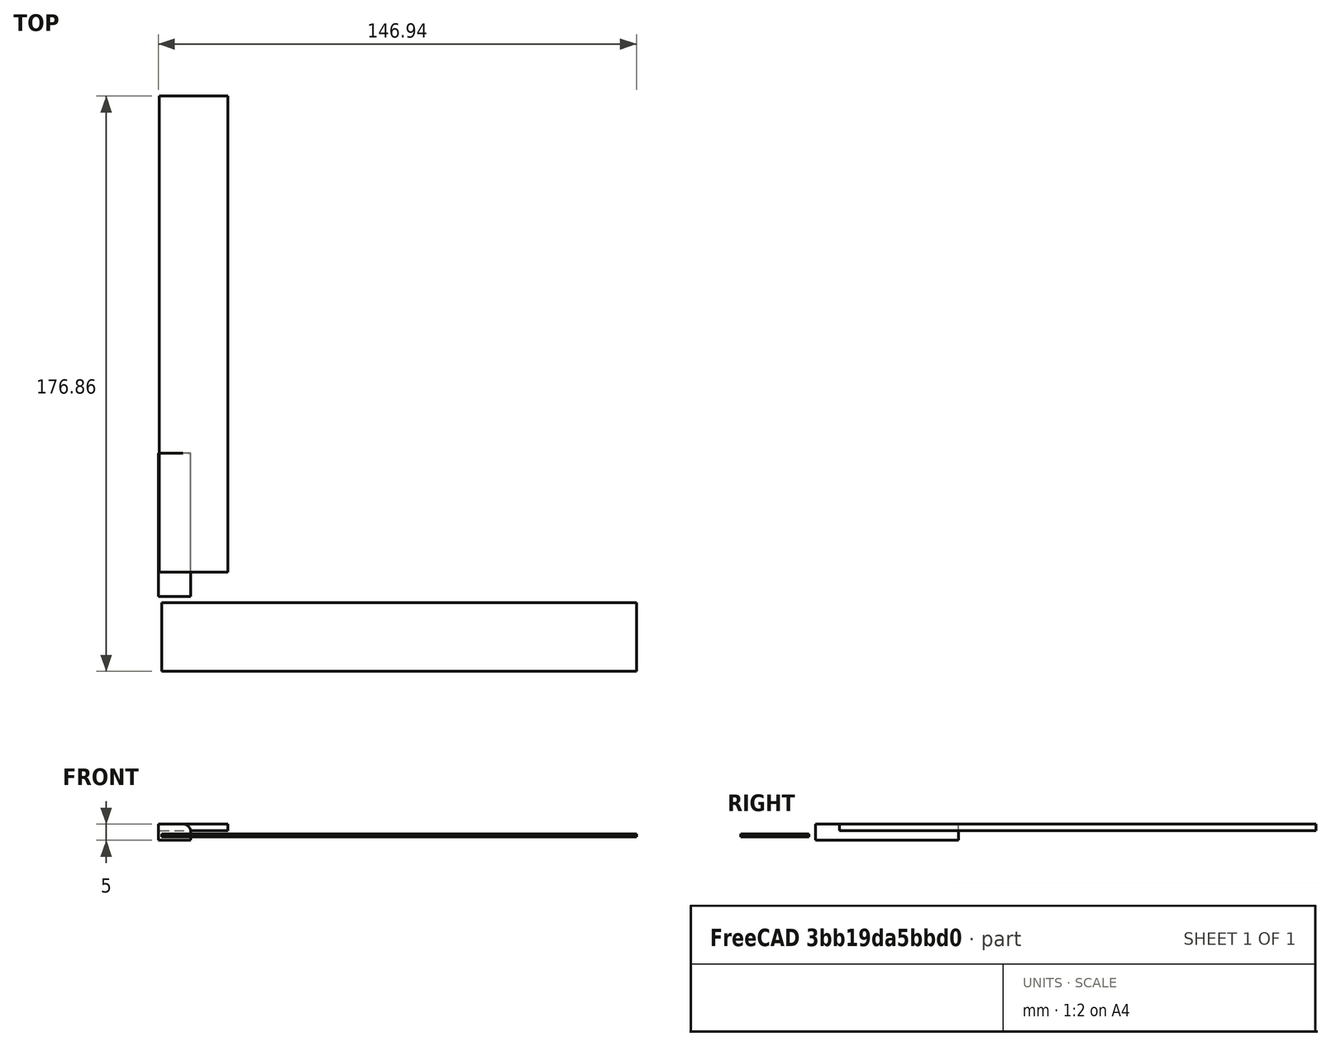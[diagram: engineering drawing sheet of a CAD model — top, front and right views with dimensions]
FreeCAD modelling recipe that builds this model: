
FCSTD DOCUMENT  (FreeCAD 0.18R4 (GitTag))
Label: UhrzeitImKlartext
License: All rights reserved
LicenseURL: http://en.wikipedia.org/wiki/All_rights_reserved
objects: Path::FeaturePython×6, Part::Part2DObjectPython×4, App::FeaturePython×2, App::DocumentObjectGroup×2, Part::FeaturePython×2, Path::FeatureCompoundPython×2, Part::Box×1, Part::Fillet×1
note: 8 computed .brp shape members not serialized (recipe doc carries the construction recipe); baked Part::Feature solids carry a one-line shape summary decoded from their .brp

FEATURE [Part::Box] Box  label="Würfel"
  AttacherType = Attacher::AttachEngine3D
  Height = 5
  Length = 10
  Width = 44
FEATURE [Part::Fillet] Fillet
  Base = -> Box
  Edges = 1 edges r=2.5: [Edge6]
FEATURE [Part::Part2DObjectPython] ShapeString  # Draft 2D object (typed FeaturePython)
  FontFile = <path>
  MapMode = 5
  Placement = pos=(4.93,7.28,6) rot=(0,0,1;1.5708rad)
  Size = 20
  String = EINS ZWEI
  Tracking = 2
FEATURE [App::FeaturePython] SetupSheet  # Path/CAM operation (typed FeaturePython)
  ClearanceHeightExpression = OpStockZMax+SetupSheet.ClearanceHeightOffset
  ClearanceHeightOffset = 5
  FinalDepthExpression = OpFinalDepth
  HorizRapid = 0
  SafeHeightExpression = OpStockZMax+SetupSheet.SafeHeightOffset
  SafeHeightOffset = 3
  StartDepthExpression = OpStartDepth
  StepDownExpression = OpToolDiameter
  VertRapid = 0
FEATURE [Part::Part2DObjectPython] Clone2D  label="Model-ShapeString"  # Draft 2D object (typed FeaturePython)
  Fuse = false
  Objects = -> [ShapeString]
  PathResource = Model
  Placement = pos=(4.93,7.28,5) rot=(0,0,1;1.5708rad)
  Scale = (1,1,1)
FEATURE [App::DocumentObjectGroup] Model
  Group = -> [Clone2D]
FEATURE [Part::FeaturePython] Stock  # WARN: FeaturePython — macro-defined, semantics opaque (R4)
  Base = -> Model
  ExtXneg = 1
  ExtXpos = 1
  ExtYneg = 1
  ExtYpos = 1
  ExtZneg = 2
  ExtZpos = 0
  Placement = pos=(1.346,8.4592,5) rot=(0,0,1;0rad)
  StockType = FromBase
FEATURE [Path::FeaturePython] T1__Fr__sbohrer_2mm  label="T1: Fräsbohrer 2mm"  # Path/CAM operation (typed FeaturePython)
  HorizFeed = 0
  HorizRapid = 0
  SpindleDir = 0
  SpindleSpeed = 0
  ToolNumber = 1
  VertFeed = 0
  VertRapid = 0
  expr: HorizRapid = SetupSheet.HorizRapid
  expr: VertRapid = SetupSheet.VertRapid
FEATURE [Path::FeaturePython] Engrave001  # Path/CAM operation (typed FeaturePython)
  Active = true
  Base = -> [Clone2D]
  ClearanceHeight = 3
  FinalDepth = -3
  OpFinalDepth = 4.5
  OpStartDepth = 5
  OpStockZMax = 5
  OpStockZMin = 3
  OpToolDiameter = 2
  SafeHeight = 3
  StartDepth = 0
  StartVertex = 0
  StepDown = 0.5
  ToolController = -> T1__Fr__sbohrer_2mm
FEATURE [Path::FeatureCompoundPython] Operations  # Path/CAM operation (typed FeaturePython)
  Group = -> [Engrave001]
  UsePlacements = false
FEATURE [Path::FeaturePython] Job  label="jobEinsZwei"  # Path/CAM operation (typed FeaturePython)
  GeometryTolerance = 0.01
  Model = -> Model
  Operations = -> Operations
  PostProcessor = 4
  SetupSheet = -> SetupSheet
  Stock = -> Stock
  ToolController = -> [T1__Fr__sbohrer_2mm]
FEATURE [Part::Part2DObjectPython] ShapeString001  # Draft 2D object (typed FeaturePython)
  FontFile = <path>
  MapMode = 5
  Placement = pos=(0,-22,2) rot=(0,0,1;0rad)
  Size = 20
  String = DREI VIER
  Tracking = 2
FEATURE [App::FeaturePython] SetupSheet001  # Path/CAM operation (typed FeaturePython)
  ClearanceHeightExpression = OpStockZMax+SetupSheet001.ClearanceHeightOffset
  ClearanceHeightOffset = 5
  FinalDepthExpression = OpFinalDepth
  HorizRapid = 0
  SafeHeightExpression = OpStockZMax+SetupSheet001.SafeHeightOffset
  SafeHeightOffset = 3
  StartDepthExpression = OpStartDepth
  StepDownExpression = OpToolDiameter
  VertRapid = 0
FEATURE [Part::Part2DObjectPython] Clone2D001  label="Model-ShapeString001"  # Draft 2D object (typed FeaturePython)
  Fuse = false
  Objects = -> [ShapeString001]
  PathResource = Model
  Placement = pos=(0,-22,2) rot=(0,0,1;0rad)
  Scale = (1,1,1)
FEATURE [App::DocumentObjectGroup] Model001
  Group = -> [Clone2D001]
FEATURE [Part::FeaturePython] Stock001  # WARN: FeaturePython — macro-defined, semantics opaque (R4)
  Base = -> Model001
  ExtXneg = 1
  ExtXpos = 1
  ExtYneg = 1
  ExtYpos = 1
  ExtZneg = 0
  ExtZpos = 0
  Placement = pos=(2.01274,-22,2) rot=(0,0,1;0rad)
  StockType = FromBase
FEATURE [Path::FeaturePython] T1__Fr__sbohrer_2mm001  label="T1: Fräsbohrer 2mm001"  # Path/CAM operation (typed FeaturePython)
  HorizFeed = 0
  HorizRapid = 0
  SpindleDir = 0
  SpindleSpeed = 1000
  ToolNumber = 1
  VertFeed = 0
  VertRapid = 0
  expr: HorizRapid = SetupSheet001.HorizRapid
  expr: VertRapid = SetupSheet001.VertRapid
FEATURE [Path::FeaturePython] Engrave  # Path/CAM operation (typed FeaturePython)
  Active = true
  Base = -> [Clone2D001]
  ClearanceHeight = 7
  FinalDepth = -3
  OpFinalDepth = 1.5
  OpStartDepth = 2
  OpStockZMax = 2
  OpStockZMin = 1
  OpToolDiameter = 2
  SafeHeight = 5
  StartDepth = 0
  StartVertex = 0
  StepDown = 0.5
  ToolController = -> T1__Fr__sbohrer_2mm001
  expr: ClearanceHeight = OpStockZMax + SetupSheet001.ClearanceHeightOffset
  expr: SafeHeight = OpStockZMax + SetupSheet001.SafeHeightOffset
FEATURE [Path::FeatureCompoundPython] Operations001  # Path/CAM operation (typed FeaturePython)
  Group = -> [Engrave]
  UsePlacements = false
FEATURE [Path::FeaturePython] Job001  label="jobDreiVier"  # Path/CAM operation (typed FeaturePython)
  GeometryTolerance = 0.01
  Model = -> Model001
  Operations = -> Operations001
  PostProcessor = 1
  SetupSheet = -> SetupSheet001
  Stock = -> Stock001
  ToolController = -> [T1__Fr__sbohrer_2mm001]
note: 2 file-system paths scrubbed to <path> (originals preserved in the JSON sidecar)
